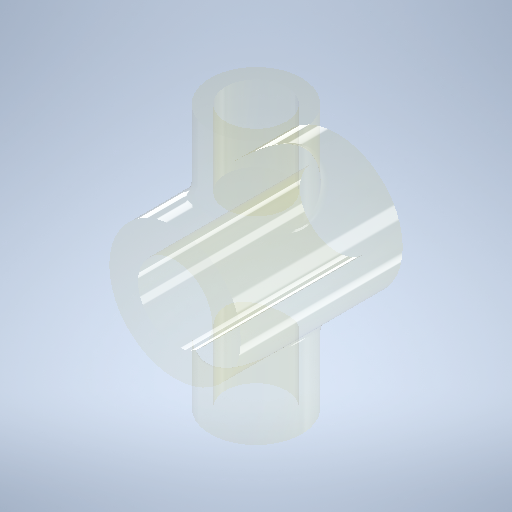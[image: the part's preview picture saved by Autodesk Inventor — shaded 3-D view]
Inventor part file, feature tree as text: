
AUTODESK INVENTOR PART (.ipt)
format: ipt  version: 2025.1 (Build 291241000, 241)  size: 372,736 bytes
history: native  units: mm
features: sketch x4, revolve x2, extrude x2, fillet x1
ambient origin geometry x8: Origin, YZ Plane, XZ Plane, XY Plane, X Axis, Y Axis, Z Axis, Center Point
bodies: Solid2 (feature_tree)
feature tree (9):
  revolve  "Revolution1"  [1 undecoded]
  revolve  "Revolution2"  [1 undecoded]
  extrude  "Extrusion8"  Depth=16.0mm
  extrude  "Extrusion9"  Depth=13.0mm
  fillet  "Congé1"  [1 undecoded]
  sketch  "Sketch8"  dims[d26=26.0mm d27=16.0mm]
  sketch  "Sketch9"  dims[d28=9.0mm d29=6.0mm]
  sketch  "Sketch10"  dims[d30=90.0deg d31=16.0mm]
  sketch  "Sketch11"  dims[d32=16.0mm d33=13.0mm d34=90.0deg d35=14.65mm d36=0.0mm d37=0.0mm d38=15.0mm d39=0.0mm d40=2.0mm]
note: 3 required parameter values undecoded (feature->parameter linkage not recoverable at this tier; creation-order binding heuristic only, values carry confidence <= 0.55)